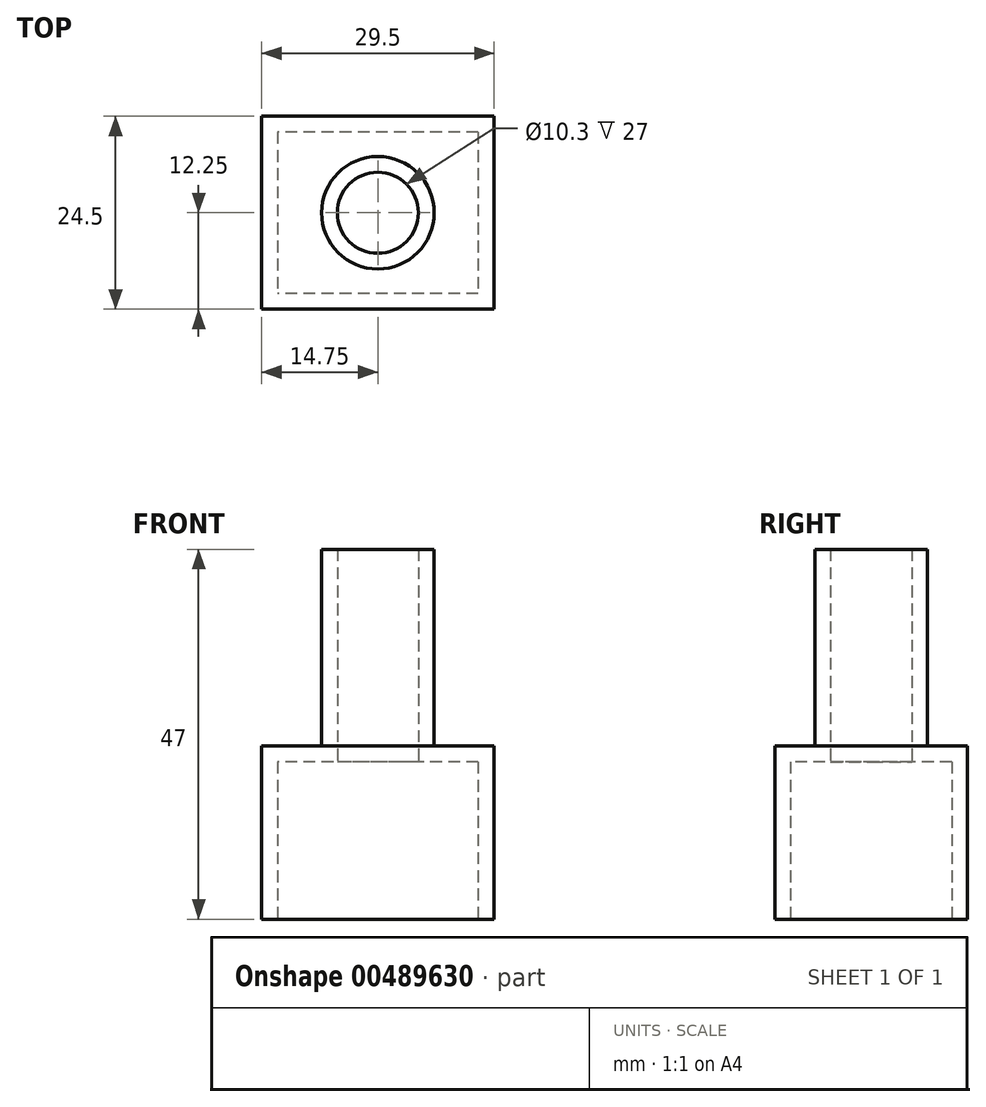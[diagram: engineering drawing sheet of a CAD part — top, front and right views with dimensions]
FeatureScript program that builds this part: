
annotation { "Feature Type Name" : "Feature", "Feature Type Description" : "" }
export const myFeature = defineFeature(function(context is Context, id is Id, definition is map)
    precondition{}
    {
        {
            var Q0;
            Q0=qCreatedBy(makeId("Top.planeOp"),FACE);
            var sketch = newSketch(context, id + "F0", { "sketchPlane" : qUnion([Q0])});
            skLineSegment(sketch, "E0.bottom", {"start": v(12.75, 10.25) * mm, "end": v(-12.75, 10.25) * mm});
            skLineSegment(sketch, "E0.top", {"start": v(12.75, -10.25) * mm, "end": v(-12.75, -10.25) * mm});
            skLineSegment(sketch, "E0.left", {"start": v(12.75, 10.25) * mm, "end": v(12.75, -10.25) * mm});
            skLineSegment(sketch, "E0.right", {"start": v(-12.75, 10.25) * mm, "end": v(-12.75, -10.25) * mm});
            skPoint(sketch, "E0.middle", {"position": v(0, 0) * mm});
            skLineSegment(sketch, "E1.bottom", {"start": v(14.75, 12.25) * mm, "end": v(-14.75, 12.25) * mm});
            skLineSegment(sketch, "E1.top", {"start": v(14.75, -12.25) * mm, "end": v(-14.75, -12.25) * mm});
            skLineSegment(sketch, "E1.left", {"start": v(14.75, 12.25) * mm, "end": v(14.75, -12.25) * mm});
            skLineSegment(sketch, "E1.right", {"start": v(-14.75, 12.25) * mm, "end": v(-14.75, -12.25) * mm});
            skSolve(sketch);
        }
        {
            var Q0;
            Q0 = qSketchRegion(id + "F0", true);
            extrude(context, id + "F1", {"entities" : qUnion([Q0]), "depth" : 20 * mm, "offsetDistance" : 25 * mm});
        }
        {
            var Q0;
            Q0=makeQuery(id+"F1.opExtrude","CAP_FACE",FACE,{"disambiguationData":[OSD([sQuery(id+"F0.wireOp",EDGE,"E0.bottom"),sQuery(id+"F0.wireOp",EDGE,"E0.top"),sQuery(id+"F0.wireOp",EDGE,"E0.left"),sQuery(id+"F0.wireOp",EDGE,"E0.right"),sQuery(id+"F0.wireOp",EDGE,"E1.bottom"),sQuery(id+"F0.wireOp",EDGE,"E1.top"),sQuery(id+"F0.wireOp",EDGE,"E1.left"),sQuery(id+"F0.wireOp",EDGE,"E1.right")])],"isStart":false});
            var sketch = newSketch(context, id + "F2", { "sketchPlane" : qUnion([Q0])});
            skLineSegment(sketch, "E2.bottom", {"start": v(14.75, -12.25) * mm, "end": v(-14.75, -12.25) * mm});
            skLineSegment(sketch, "E2.top", {"start": v(14.75, 12.25) * mm, "end": v(-14.75, 12.25) * mm});
            skLineSegment(sketch, "E2.left", {"start": v(14.75, -12.25) * mm, "end": v(14.75, 12.25) * mm});
            skLineSegment(sketch, "E2.right", {"start": v(-14.75, -12.25) * mm, "end": v(-14.75, 12.25) * mm});
            skPoint(sketch, "E2.middle", {"position": v(0, 0) * mm});
            skSolve(sketch);
        }
        {
            var Q0;
            Q0 = qSketchRegion(id + "F2", true);
            extrude(context, id + "F3", {"entities" : qUnion([Q0]), "operationType" : NewBodyOperationType.ADD, "depth" : 2 * mm, "offsetDistance" : 25 * mm});
        }
        {
            var Q0;
            Q0=makeQuery(id+"F3.opExtrude","CAP_FACE",FACE,{"disambiguationData":[OSD([sQuery(id+"F2.wireOp",EDGE,"E2.bottom"),sQuery(id+"F2.wireOp",EDGE,"E2.top"),sQuery(id+"F2.wireOp",EDGE,"E2.left"),sQuery(id+"F2.wireOp",EDGE,"E2.right")])],"isStart":false});
            var sketch = newSketch(context, id + "F4", { "sketchPlane" : qUnion([Q0])});
            skCircle(sketch, "E3", {"center": v(0, 0) * mm, "radius": 5.15 * mm});
            skCircle(sketch, "E4.0", {"center": v(0, 0) * mm, "radius": 7.15 * mm});
            skSolve(sketch);
        }
        {
            var Q0;
            Q0 = qSketchRegion(id + "F4", true);
            extrude(context, id + "F5", {"entities" : qUnion([Q0]), "operationType" : NewBodyOperationType.ADD, "depth" : 25 * mm, "offsetDistance" : 25 * mm});
        }
        {
            var Q0;
            Q0=makeQuery(id+"F5.boolean.opBoolean","SPLIT",FACE,{"disambiguationData":[TD([makeQuery(id+"F5.opExtrude","SWEPT_FACE",FACE,{"disambiguationData":[OSD([sQuery(id+"F4.wireOp",EDGE,"E3")])]})])],"derivedFrom":makeQuery(id+"F3.opExtrude","CAP_FACE",FACE,{"disambiguationData":[OSD([sQuery(id+"F2.wireOp",EDGE,"E2.bottom"),sQuery(id+"F2.wireOp",EDGE,"E2.top"),sQuery(id+"F2.wireOp",EDGE,"E2.left"),sQuery(id+"F2.wireOp",EDGE,"E2.right")])],"isStart":false})});
            extrude(context, id + "F6", {"entities" : qUnion([Q0]), "operationType" : NewBodyOperationType.REMOVE, "oppositeDirection" : true, "depth" : 25 * mm, "offsetDistance" : 25 * mm});
        }
    });
